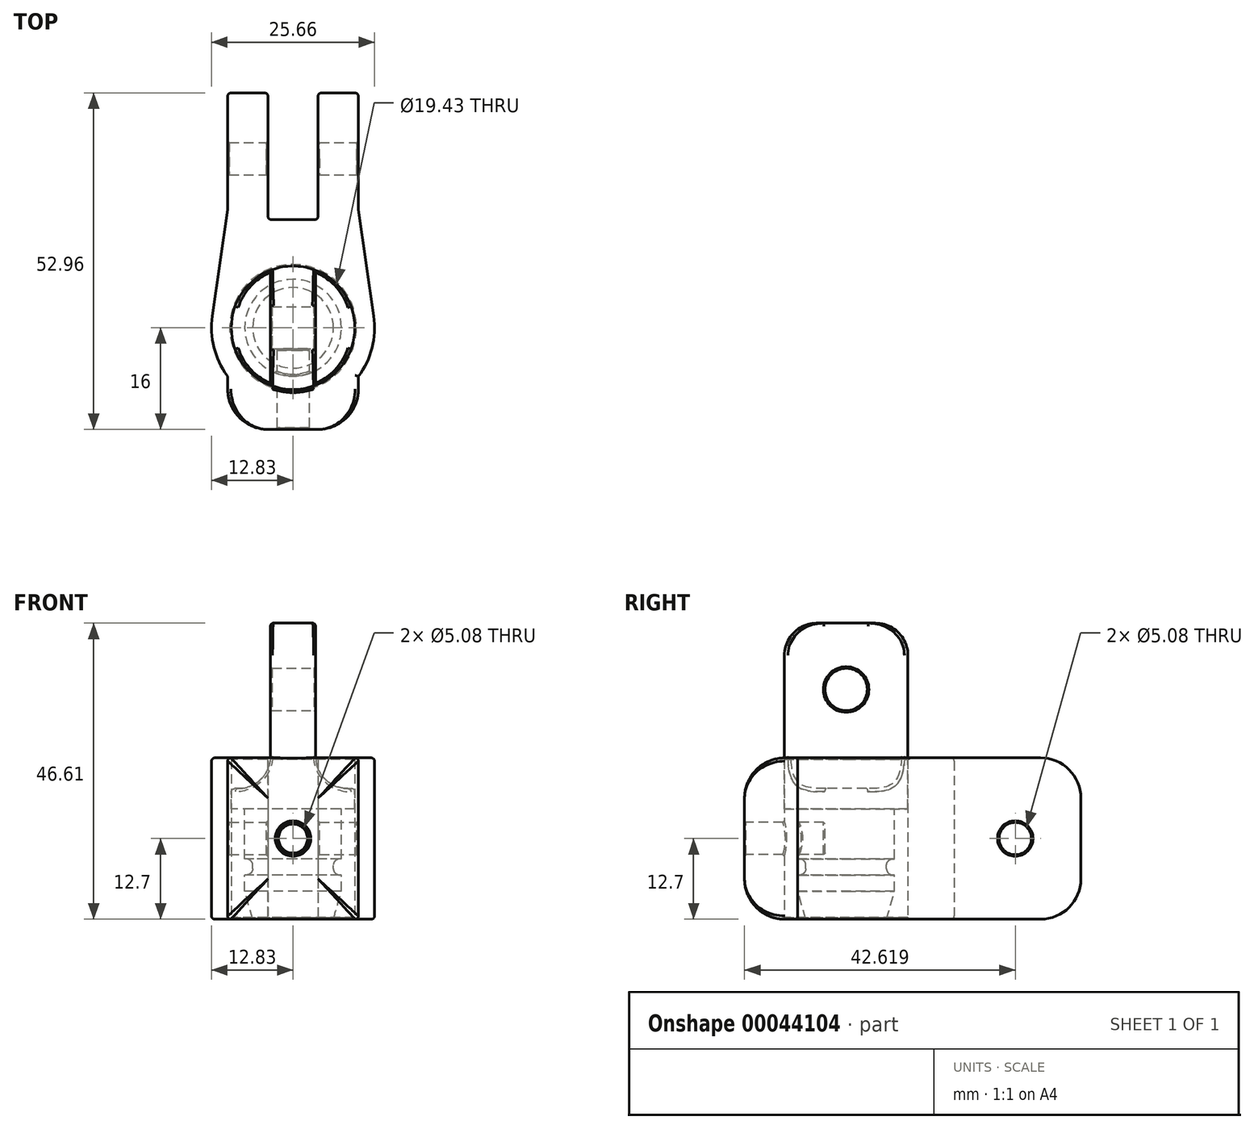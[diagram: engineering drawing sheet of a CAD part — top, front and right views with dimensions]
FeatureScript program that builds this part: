
annotation { "Feature Type Name" : "Feature", "Feature Type Description" : "" }
export const myFeature = defineFeature(function(context is Context, id is Id, definition is map)
    precondition{}
    {
        {
            var Q0;
            Q0=qCreatedBy(makeId("Front.planeOp"),FACE);
            var sketch = newSketch(context, id + "F0", { "sketchPlane" : qUnion([Q0])});
            skLineSegment(sketch, "E0", {"start": v(0, 0) * mm, "end": v(-6.35, 0) * mm});
            skLineSegment(sketch, "E1", {"start": v(-6.35, 0) * mm, "end": v(-7.62, 4.42) * mm});
            skLineSegment(sketch, "E2", {"start": v(-7.62, 4.42) * mm, "end": v(-7.62, 6.96) * mm});
            skLineSegment(sketch, "E3", {"start": v(-7.62, 6.96) * mm, "end": v(-7.37, 6.96) * mm});
            skLineSegment(sketch, "E4", {"start": v(-6.35, 7.98) * mm, "end": v(-6.35, 8.48) * mm});
            skLineSegment(sketch, "E5", {"start": v(-7.37, 9.5) * mm, "end": v(-7.62, 9.5) * mm});
            skLineSegment(sketch, "E6", {"start": v(-7.62, 9.5) * mm, "end": v(-7.62, 17.37) * mm});
            skLineSegment(sketch, "E7", {"start": v(0, 17.37) * mm, "end": v(-9.72, 17.37) * mm});
            skLineSegment(sketch, "E8", {"start": v(-9.72, 17.37) * mm, "end": v(-9.72, 37.08) * mm});
            skLineSegment(sketch, "E9", {"start": v(0, 46.6) * mm, "end": v(0, 46.6) * mm});
            skLineSegment(sketch, "E10", {"start": v(0, 46.6) * mm, "end": v(0, 0) * mm});
            skPoint(sketch, "E11.visualSharp", {"position": v(-9.72, 46.6) * mm});
            skPoint(sketch, "E12.visualSharp", {"position": v(-6.35, 9.5) * mm});
            skArc(sketch, "E12.filletArc", {"start": v(-6.35, 8.48) * mm, "mid": v(-6.65, 9.2) * mm, "end": v(-7.37, 9.5) * mm});
            skPoint(sketch, "E13.visualSharp", {"position": v(-6.35, 6.96) * mm});
            skArc(sketch, "E13.filletArc", {"start": v(-7.37, 6.96) * mm, "mid": v(-6.65, 7.26) * mm, "end": v(-6.35, 7.98) * mm});
            skLineSegment(sketch, "E14", {"start": v(0, 46.6) * mm, "end": v(-9.72, 46.6) * mm});
            skLineSegment(sketch, "E15", {"start": v(-9.72, 37.08) * mm, "end": v(-9.72, 46.6) * mm});
            skLineSegment(sketch, "E16", {"start": v(9.91, 20.55) * mm, "end": v(-9.72, 20.55) * mm, "construction": true});
            skSolve(sketch);
        }
        {
            var Q0;
            {var subQ4=sQuery(id+"F0.wireOp",EDGE,"E0");Q0=makeQuery(id+"F0.imprint","IMPRINT",FACE,{"disambiguationData":[TD([[makeQuery(id+"F0.imprint","IMPRINT",EDGE,{"derivedFrom":subQ4}),-1.0]])]});}
            var Q1;
            {var subQ0=sQuery(id+"F0.wireOp",EDGE,"E16");Q1=makeQuery(id+"F0.imprint","IMPRINT",FACE,{"disambiguationData":[TD([[makeQuery(id+"F0.imprint","IMPRINT",EDGE,{"derivedFrom":subQ0}),1.0]])]});}
            var Q2;
            {var subQ4=sQuery(id+"F0.wireOp",EDGE,"E14");Q2=makeQuery(id+"F0.imprint","IMPRINT",FACE,{"disambiguationData":[TD([[makeQuery(id+"F0.imprint","IMPRINT",EDGE,{"derivedFrom":subQ4}),1.0]])]});}
            var Q3;
            Q3=sQuery(id+"F0.wireOp",EDGE,"E10");
            revolve(context, id + "F1", {"entities" : qUnion([Q0, Q1, Q2]), "axis" : qUnion([Q3]), "revolveType" : RevolveType.FULL});
        }
        {
            var Q0;
            Q0=qCreatedBy(makeId("Front.planeOp"),FACE);
            var sketch = newSketch(context, id + "F2", { "sketchPlane" : qUnion([Q0])});
            skLineSegment(sketch, "E17.bottom", {"start": v(3.56, 48.33) * mm, "end": v(17.07, 48.33) * mm});
            skLineSegment(sketch, "E17.top", {"start": v(8.64, 20.57) * mm, "end": v(17.07, 20.57) * mm});
            skLineSegment(sketch, "E17.left", {"start": v(3.56, 48.33) * mm, "end": v(3.56, 25.65) * mm});
            skLineSegment(sketch, "E17.right", {"start": v(17.07, 48.33) * mm, "end": v(17.07, 20.57) * mm});
            skPoint(sketch, "E18.visualSharp", {"position": v(3.56, 20.57) * mm});
            skArc(sketch, "E18.filletArc", {"start": v(3.56, 25.65) * mm, "mid": v(5.04, 22.05) * mm, "end": v(8.64, 20.57) * mm});
            skLineSegment(sketch, "E19.MirrorCS", {"start": v(-3.56, 48.33) * mm, "end": v(-3.56, 25.65) * mm});
            skArc(sketch, "E20.MirrorCS", {"start": v(-3.56, 25.65) * mm, "mid": v(-5.04, 22.05) * mm, "end": v(-8.64, 20.57) * mm});
            skLineSegment(sketch, "E21.MirrorCS", {"start": v(-8.64, 20.57) * mm, "end": v(-17.07, 20.57) * mm});
            skLineSegment(sketch, "E22.MirrorCS", {"start": v(-17.07, 48.33) * mm, "end": v(-17.07, 20.57) * mm});
            skLineSegment(sketch, "E23.MirrorCS", {"start": v(-3.56, 48.33) * mm, "end": v(-17.07, 48.33) * mm});
            skSolve(sketch);
        }
        {
            var Q0;
            Q0 = qSketchRegion(id + "F2", true);
            extrude(context, id + "F3", {"entities" : qUnion([Q0]), "operationType" : NewBodyOperationType.REMOVE, "endBound" : BoundingType.SYMMETRIC, "oppositeDirection" : true, "depth" : 25.4 * mm});
        }
        {
            var Q0;
            Q0=makeQuery(id+"F3.boolean.opBoolean","SPLIT",EDGE,{"disambiguationData":[OD(1.0)],"derivedFrom":makeQuery(id+"F1.opRevolve","SWEPT_EDGE",EDGE,{"disambiguationData":[OSD([sQuery(id+"F0.wireOp",EDGE,"E14"),sQuery(id+"F0.wireOp",EDGE,"E15")])]})});
            var Q1;
            Q1=makeQuery(id+"F3.boolean.opBoolean","SPLIT",EDGE,{"disambiguationData":[OD(0.0)],"derivedFrom":makeQuery(id+"F1.opRevolve","SWEPT_EDGE",EDGE,{"disambiguationData":[OSD([sQuery(id+"F0.wireOp",EDGE,"E14"),sQuery(id+"F0.wireOp",EDGE,"E15")])]})});
            fillet(context, id + "F4", {"entities" : qUnion([Q0, Q1]), "radius" : 5.08 * mm, "tangentPropagation" : true, "allowEdgeOverflow" : false});
        }
        {
            var Q0;
            Q0=qCreatedBy(makeId("Right.planeOp"),FACE);
            var sketch = newSketch(context, id + "F5", { "sketchPlane" : qUnion([Q0])});
            skCircle(sketch, "E24", {"center": v(0, 36.17) * mm, "radius": 3.33 * mm});
            skSolve(sketch);
        }
        {
            var Q0;
            Q0 = qSketchRegion(id + "F5", true);
            extrude(context, id + "F6", {"entities" : qUnion([Q0]), "operationType" : NewBodyOperationType.REMOVE, "endBound" : BoundingType.SYMMETRIC, "oppositeDirection" : true, "depth" : 42.5 * mm});
        }
        {
            var Q0;
            Q0=makeQuery(id+"F6.boolean.opBoolean","COPY",FACE,{"derivedFrom":makeQuery(id+"F6.opExtrude","SWEPT_FACE",FACE,{"disambiguationData":[OSD([sQuery(id+"F5.wireOp",EDGE,"E24")])]})});
            chamfer(context, id + "F7", {"entities" : qUnion([Q0]), "width" : 0.25 * mm, "tangentPropagation" : true});
        }
        {
            var Q0;
            Q0=makeQuery(id+"F3.boolean.opBoolean","INTERSECT",EDGE,{"disambiguationData":[OD(1.0)],"derivedFrom":[makeQuery(id+"F1.opRevolve","SWEPT_FACE",FACE,{"disambiguationData":[OSD([sQuery(id+"F0.wireOp",EDGE,"E8"),sQuery(id+"F0.wireOp",EDGE,"E15")])]}),makeQuery(id+"F3.opExtrude","SWEPT_FACE",FACE,{"disambiguationData":[OSD([sQuery(id+"F2.wireOp",EDGE,"E18.filletArc")])]})]});
            var Q1;
            Q1=makeQuery(id+"F3.boolean.opBoolean","INTERSECT",EDGE,{"disambiguationData":[OD(1.0)],"derivedFrom":[makeQuery(id+"F1.opRevolve","SWEPT_FACE",FACE,{"disambiguationData":[OSD([sQuery(id+"F0.wireOp",EDGE,"E8"),sQuery(id+"F0.wireOp",EDGE,"E15")])]}),makeQuery(id+"F3.opExtrude","SWEPT_FACE",FACE,{"disambiguationData":[OSD([sQuery(id+"F2.wireOp",EDGE,"E17.left")])]})]});
            var Q2;
            Q2=makeQuery(id+"F4.opFillet","BLEND_EDGE",EDGE,{"blendedFrom":[makeQuery(id+"F3.boolean.opBoolean","SPLIT",EDGE,{"disambiguationData":[OD(1.0)],"derivedFrom":makeQuery(id+"F1.opRevolve","SWEPT_EDGE",EDGE,{"disambiguationData":[OSD([sQuery(id+"F0.wireOp",EDGE,"E14"),sQuery(id+"F0.wireOp",EDGE,"E15")])]})}),makeQuery(id+"F3.boolean.opBoolean","COPY",FACE,{"derivedFrom":makeQuery(id+"F3.opExtrude","SWEPT_FACE",FACE,{"disambiguationData":[OSD([sQuery(id+"F2.wireOp",EDGE,"E17.left")])]})})],"blendedInto":[makeQuery(id+"F3.boolean.opBoolean","COPY",FACE,{"derivedFrom":makeQuery(id+"F3.opExtrude","SWEPT_FACE",FACE,{"disambiguationData":[OSD([sQuery(id+"F2.wireOp",EDGE,"E17.left")])]})})]});
            var Q3;
            Q3=makeQuery(id+"F3.boolean.opBoolean","INTERSECT",EDGE,{"derivedFrom":[makeQuery(id+"F1.opRevolve","SWEPT_FACE",FACE,{"disambiguationData":[OSD([sQuery(id+"F0.wireOp",EDGE,"E14")])]}),makeQuery(id+"F3.opExtrude","SWEPT_FACE",FACE,{"disambiguationData":[OSD([sQuery(id+"F2.wireOp",EDGE,"E17.left")])]})]});
            var Q4;
            {var subQ0=sQuery(id+"F0.wireOp",EDGE,"E14");Q4=makeQuery(id+"F4.opFillet","BLEND_EDGE",EDGE,{"blendedFrom":[makeQuery(id+"F3.boolean.opBoolean","SPLIT",EDGE,{"disambiguationData":[OD(0.0)],"derivedFrom":makeQuery(id+"F1.opRevolve","SWEPT_EDGE",EDGE,{"disambiguationData":[OSD([subQ0,sQuery(id+"F0.wireOp",EDGE,"E15")])]})}),makeQuery(id+"F1.opRevolve","SWEPT_FACE",FACE,{"disambiguationData":[OSD([subQ0])]})],"blendedInto":[makeQuery(id+"F1.opRevolve","SWEPT_FACE",FACE,{"disambiguationData":[OSD([subQ0])]})]});}
            var Q5;
            Q5=makeQuery(id+"F4.opFillet","BLEND_EDGE",EDGE,{"blendedFrom":[makeQuery(id+"F3.boolean.opBoolean","SPLIT",EDGE,{"disambiguationData":[OD(0.0)],"derivedFrom":makeQuery(id+"F1.opRevolve","SWEPT_EDGE",EDGE,{"disambiguationData":[OSD([sQuery(id+"F0.wireOp",EDGE,"E14"),sQuery(id+"F0.wireOp",EDGE,"E15")])]})}),makeQuery(id+"F3.boolean.opBoolean","COPY",FACE,{"derivedFrom":makeQuery(id+"F3.opExtrude","SWEPT_FACE",FACE,{"disambiguationData":[OSD([sQuery(id+"F2.wireOp",EDGE,"E19.MirrorCS")])]})})],"blendedInto":[makeQuery(id+"F3.boolean.opBoolean","COPY",FACE,{"derivedFrom":makeQuery(id+"F3.opExtrude","SWEPT_FACE",FACE,{"disambiguationData":[OSD([sQuery(id+"F2.wireOp",EDGE,"E19.MirrorCS")])]})})]});
            var Q6;
            Q6=makeQuery(id+"F3.boolean.opBoolean","INTERSECT",EDGE,{"disambiguationData":[OD(0.0)],"derivedFrom":[makeQuery(id+"F1.opRevolve","SWEPT_FACE",FACE,{"disambiguationData":[OSD([sQuery(id+"F0.wireOp",EDGE,"E8"),sQuery(id+"F0.wireOp",EDGE,"E15")])]}),makeQuery(id+"F3.opExtrude","SWEPT_FACE",FACE,{"disambiguationData":[OSD([sQuery(id+"F2.wireOp",EDGE,"E19.MirrorCS")])]})]});
            var Q7;
            Q7=makeQuery(id+"F3.boolean.opBoolean","INTERSECT",EDGE,{"disambiguationData":[OD(0.0)],"derivedFrom":[makeQuery(id+"F1.opRevolve","SWEPT_FACE",FACE,{"disambiguationData":[OSD([sQuery(id+"F0.wireOp",EDGE,"E8"),sQuery(id+"F0.wireOp",EDGE,"E15")])]}),makeQuery(id+"F3.opExtrude","SWEPT_FACE",FACE,{"disambiguationData":[OSD([sQuery(id+"F2.wireOp",EDGE,"E20.MirrorCS")])]})]});
            var Q8;
            Q8=makeQuery(id+"F4.opFillet","BLEND_EDGE",EDGE,{"blendedFrom":[makeQuery(id+"F3.boolean.opBoolean","SPLIT",EDGE,{"disambiguationData":[OD(0.0)],"derivedFrom":makeQuery(id+"F1.opRevolve","SWEPT_EDGE",EDGE,{"disambiguationData":[OSD([sQuery(id+"F0.wireOp",EDGE,"E14"),sQuery(id+"F0.wireOp",EDGE,"E15")])]})}),makeQuery(id+"F3.boolean.opBoolean","COPY",FACE,{"derivedFrom":makeQuery(id+"F3.opExtrude","SWEPT_FACE",FACE,{"disambiguationData":[OSD([sQuery(id+"F2.wireOp",EDGE,"E17.left")])]})})],"blendedInto":[makeQuery(id+"F3.boolean.opBoolean","COPY",FACE,{"derivedFrom":makeQuery(id+"F3.opExtrude","SWEPT_FACE",FACE,{"disambiguationData":[OSD([sQuery(id+"F2.wireOp",EDGE,"E17.left")])]})})]});
            var Q9;
            Q9=makeQuery(id+"F3.boolean.opBoolean","INTERSECT",EDGE,{"disambiguationData":[OD(0.0)],"derivedFrom":[makeQuery(id+"F1.opRevolve","SWEPT_FACE",FACE,{"disambiguationData":[OSD([sQuery(id+"F0.wireOp",EDGE,"E8"),sQuery(id+"F0.wireOp",EDGE,"E15")])]}),makeQuery(id+"F3.opExtrude","SWEPT_FACE",FACE,{"disambiguationData":[OSD([sQuery(id+"F2.wireOp",EDGE,"E18.filletArc")])]})]});
            var Q10;
            Q10=makeQuery(id+"F3.boolean.opBoolean","INTERSECT",EDGE,{"disambiguationData":[OD(0.0)],"derivedFrom":[makeQuery(id+"F1.opRevolve","SWEPT_FACE",FACE,{"disambiguationData":[OSD([sQuery(id+"F0.wireOp",EDGE,"E8"),sQuery(id+"F0.wireOp",EDGE,"E15")])]}),makeQuery(id+"F3.opExtrude","SWEPT_FACE",FACE,{"disambiguationData":[OSD([sQuery(id+"F2.wireOp",EDGE,"E17.left")])]})]});
            var Q11;
            Q11=makeQuery(id+"F3.boolean.opBoolean","INTERSECT",EDGE,{"disambiguationData":[OD(1.0)],"derivedFrom":[makeQuery(id+"F1.opRevolve","SWEPT_FACE",FACE,{"disambiguationData":[OSD([sQuery(id+"F0.wireOp",EDGE,"E8"),sQuery(id+"F0.wireOp",EDGE,"E15")])]}),makeQuery(id+"F3.opExtrude","SWEPT_FACE",FACE,{"disambiguationData":[OSD([sQuery(id+"F2.wireOp",EDGE,"E20.MirrorCS")])]})]});
            var Q12;
            Q12=makeQuery(id+"F3.boolean.opBoolean","INTERSECT",EDGE,{"disambiguationData":[OD(1.0)],"derivedFrom":[makeQuery(id+"F1.opRevolve","SWEPT_FACE",FACE,{"disambiguationData":[OSD([sQuery(id+"F0.wireOp",EDGE,"E8"),sQuery(id+"F0.wireOp",EDGE,"E15")])]}),makeQuery(id+"F3.opExtrude","SWEPT_FACE",FACE,{"disambiguationData":[OSD([sQuery(id+"F2.wireOp",EDGE,"E19.MirrorCS")])]})]});
            var Q13;
            Q13=makeQuery(id+"F4.opFillet","BLEND_EDGE",EDGE,{"blendedFrom":[makeQuery(id+"F3.boolean.opBoolean","SPLIT",EDGE,{"disambiguationData":[OD(1.0)],"derivedFrom":makeQuery(id+"F1.opRevolve","SWEPT_EDGE",EDGE,{"disambiguationData":[OSD([sQuery(id+"F0.wireOp",EDGE,"E14"),sQuery(id+"F0.wireOp",EDGE,"E15")])]})}),makeQuery(id+"F3.boolean.opBoolean","COPY",FACE,{"derivedFrom":makeQuery(id+"F3.opExtrude","SWEPT_FACE",FACE,{"disambiguationData":[OSD([sQuery(id+"F2.wireOp",EDGE,"E19.MirrorCS")])]})})],"blendedInto":[makeQuery(id+"F3.boolean.opBoolean","COPY",FACE,{"derivedFrom":makeQuery(id+"F3.opExtrude","SWEPT_FACE",FACE,{"disambiguationData":[OSD([sQuery(id+"F2.wireOp",EDGE,"E19.MirrorCS")])]})})]});
            fillet(context, id + "F8", {"entities" : qUnion([Q0, Q1, Q2, Q3, Q4, Q5, Q6, Q7, Q8, Q9, Q10, Q11, Q12, Q13]), "radius" : 0.5 * mm, "tangentPropagation" : true, "allowEdgeOverflow" : false});
        }
        {
            var Q0;
            Q0=qCreatedBy(makeId("Top.planeOp"),FACE);
            var sketch = newSketch(context, id + "F9", { "sketchPlane" : qUnion([Q0])});
            skCircle(sketch, "E25", {"center": v(0, 0) * mm, "radius": 9.72 * mm});
            skCircle(sketch, "E26", {"center": v(0, 0) * mm, "radius": 12.83 * mm});
            skLineSegment(sketch, "E27", {"start": v(-10.29, 36.96) * mm, "end": v(-3.94, 36.96) * mm});
            skLineSegment(sketch, "E28", {"start": v(-3.94, 36.96) * mm, "end": v(-3.94, 17.02) * mm});
            skLineSegment(sketch, "E29", {"start": v(-3.94, 17.02) * mm, "end": v(3.94, 17.02) * mm});
            skLineSegment(sketch, "E30", {"start": v(3.94, 17.02) * mm, "end": v(3.94, 36.96) * mm});
            skLineSegment(sketch, "E31", {"start": v(3.94, 36.96) * mm, "end": v(10.29, 36.96) * mm});
            skLineSegment(sketch, "E32", {"start": v(10.29, 36.96) * mm, "end": v(10.29, 18.64) * mm});
            skLineSegment(sketch, "E33", {"start": v(10.29, 18.64) * mm, "end": v(12.7, 1.82) * mm});
            skLineSegment(sketch, "E34.MirrorCS", {"start": v(-10.29, 36.96) * mm, "end": v(-10.29, 18.64) * mm});
            skLineSegment(sketch, "E35.MirrorCS", {"start": v(-10.29, 18.64) * mm, "end": v(-12.7, 1.82) * mm});
            skLineSegment(sketch, "E36", {"start": v(-10.29, 26.57) * mm, "end": v(10.29, 26.57) * mm, "construction": true});
            skLineSegment(sketch, "E37", {"start": v(10.29, -16) * mm, "end": v(-10.29, -16) * mm});
            skLineSegment(sketch, "E38", {"start": v(-12.83, 0) * mm, "end": v(-12.83, 0) * mm});
            skLineSegment(sketch, "E39", {"start": v(12.83, 0) * mm, "end": v(12.83, 0) * mm});
            skLineSegment(sketch, "E40", {"start": v(-10.29, -7.66) * mm, "end": v(-10.29, -16) * mm});
            skLineSegment(sketch, "E41", {"start": v(10.29, -7.66) * mm, "end": v(10.29, -16) * mm});
            skSolve(sketch);
        }
        {
            var Q0;
            Q0=makeQuery(id+"F9.imprint","IMPRINT",FACE,{"disambiguationData":[TD([[makeQuery(id+"F9.imprint","IMPRINT",EDGE,{"derivedFrom":sQuery(id+"F9.wireOp",EDGE,"9beef8d4-fd38-4892-9b5a-89d50c57ea27.bottom")}),-1.0]])]});
            var Q1;
            {var subQ4=sQuery(id+"F9.wireOp",EDGE,"E27");Q1=makeQuery(id+"F9.imprint","IMPRINT",FACE,{"disambiguationData":[TD([[makeQuery(id+"F9.imprint","IMPRINT",EDGE,{"derivedFrom":subQ4}),-1.0]])]});}
            var Q2;
            Q2=makeQuery(id+"F9.imprint","IMPRINT",FACE,{"disambiguationData":[TD([[makeQuery(id+"F9.imprint","IMPRINT",EDGE,{"derivedFrom":sQuery(id+"F9.wireOp",EDGE,"E25")}),-1.0]])]});
            var Q3;
            Q3=makeQuery(id+"F9.imprint","IMPRINT",FACE,{"disambiguationData":[TD([[makeQuery(id+"F9.imprint","IMPRINT",EDGE,{"derivedFrom":sQuery(id+"F9.wireOp",EDGE,"E37")}),-1.0]])]});
            extrude(context, id + "F10", {"entities" : qUnion([Q0, Q1, Q2, Q3]), "depth" : 25.4 * mm});
        }
        {
            var Q0;
            Q0=makeQuery(id+"F10.opExtrude","SWEPT_FACE",FACE,{"disambiguationData":[OSD([sQuery(id+"F9.wireOp",EDGE,"E32")])]});
            var sketch = newSketch(context, id + "F11", { "sketchPlane" : qUnion([Q0])});
            skLineSegment(sketch, "E42", {"start": v(18.64, 12.7) * mm, "end": v(36.96, 12.7) * mm, "construction": true});
            skLineSegment(sketch, "E43", {"start": v(26.62, 25.4) * mm, "end": v(26.62, 0) * mm, "construction": true});
            skCircle(sketch, "E44", {"center": v(26.62, 12.7) * mm, "radius": 2.54 * mm});
            skSolve(sketch);
        }
        {
            var Q0;
            Q0=makeQuery(id+"F11.imprint","IMPRINT",FACE,{"disambiguationData":[TD([[makeQuery(id+"F11.imprint","IMPRINT",EDGE,{"derivedFrom":sQuery(id+"F11.wireOp",EDGE,"E44")}),1.0]])]});
            var Q1;
            Q1=sQuery(id+"F11.wireOp",EDGE,"E44");
            extrude(context, id + "F12", {"entities" : qUnion([Q0]), "operationType" : NewBodyOperationType.REMOVE, "surfaceEntities" : qUnion([Q1]), "oppositeDirection" : true, "depth" : 25.4 * mm});
        }
        {
            var Q0;
            Q0=makeQuery(id+"F10.opExtrude","SWEPT_FACE",FACE,{"disambiguationData":[OSD([sQuery(id+"F9.wireOp",EDGE,"E37")])]});
            var sketch = newSketch(context, id + "F13", { "sketchPlane" : qUnion([Q0])});
            skLineSegment(sketch, "E45", {"start": v(0, 0) * mm, "end": v(0, 25.4) * mm, "construction": true});
            skLineSegment(sketch, "E46", {"start": v(10.29, 12.7) * mm, "end": v(-10.29, 12.7) * mm, "construction": true});
            skCircle(sketch, "E47", {"center": v(0, 12.7) * mm, "radius": 2.54 * mm});
            skSolve(sketch);
        }
        {
            var Q0;
            Q0=makeQuery(id+"F13.imprint","IMPRINT",FACE,{"disambiguationData":[TD([[makeQuery(id+"F13.imprint","IMPRINT",EDGE,{"derivedFrom":sQuery(id+"F13.wireOp",EDGE,"E47")}),1.0]])]});
            extrude(context, id + "F14", {"entities" : qUnion([Q0]), "operationType" : NewBodyOperationType.REMOVE, "oppositeDirection" : true, "depth" : 12.7 * mm});
        }
        {
            var Q0;
            Q0=makeQuery(id+"F12.boolean.opBoolean","COPY",FACE,{"disambiguationData":[OD(0.0)],"derivedFrom":makeQuery(id+"F12.opExtrude","SWEPT_FACE",FACE,{"disambiguationData":[OSD([sQuery(id+"F11.wireOp",EDGE,"E44")])]})});
            var Q1;
            Q1=makeQuery(id+"F12.boolean.opBoolean","COPY",FACE,{"disambiguationData":[OD(1.0)],"derivedFrom":makeQuery(id+"F12.opExtrude","SWEPT_FACE",FACE,{"disambiguationData":[OSD([sQuery(id+"F11.wireOp",EDGE,"E44")])]})});
            var Q2;
            Q2=makeQuery(id+"F14.boolean.opBoolean","COPY",FACE,{"derivedFrom":makeQuery(id+"F14.opExtrude","SWEPT_FACE",FACE,{"disambiguationData":[OSD([sQuery(id+"F13.wireOp",EDGE,"E47")])]})});
            var Q3;
            Q3=makeQuery(id+"F10.opExtrude","SWEPT_FACE",FACE,{"disambiguationData":[OSD([sQuery(id+"F9.wireOp",EDGE,"E25")])]});
            chamfer(context, id + "F15", {"entities" : qUnion([Q0, Q1, Q2, Q3]), "width" : 0.25 * mm, "tangentPropagation" : true});
        }
        {
            var Q0;
            Q0=makeQuery(id+"F10.opExtrude","CAP_EDGE",EDGE,{"disambiguationData":[OSD([sQuery(id+"F9.wireOp",EDGE,"E27")])],"isStart":false});
            var Q1;
            Q1=makeQuery(id+"F10.opExtrude","CAP_EDGE",EDGE,{"disambiguationData":[OSD([sQuery(id+"F9.wireOp",EDGE,"E31")])],"isStart":false});
            var Q2;
            Q2=makeQuery(id+"F10.opExtrude","CAP_EDGE",EDGE,{"disambiguationData":[OSD([sQuery(id+"F9.wireOp",EDGE,"E31")])],"isStart":true});
            var Q3;
            Q3=makeQuery(id+"F10.opExtrude","CAP_EDGE",EDGE,{"disambiguationData":[OSD([sQuery(id+"F9.wireOp",EDGE,"E27")])],"isStart":true});
            var Q4;
            Q4=makeQuery(id+"F10.opExtrude","CAP_EDGE",EDGE,{"disambiguationData":[OSD([sQuery(id+"F9.wireOp",EDGE,"E37")])],"isStart":false});
            var Q5;
            Q5=makeQuery(id+"F10.opExtrude","SWEPT_EDGE",EDGE,{"disambiguationData":[OSD([sQuery(id+"F9.wireOp",EDGE,"E37"),sQuery(id+"F9.wireOp",EDGE,"E41")])]});
            var Q6;
            Q6=makeQuery(id+"F10.opExtrude","SWEPT_EDGE",EDGE,{"disambiguationData":[OSD([sQuery(id+"F9.wireOp",EDGE,"E37"),sQuery(id+"F9.wireOp",EDGE,"E40")])]});
            var Q7;
            Q7=makeQuery(id+"F10.opExtrude","CAP_EDGE",EDGE,{"disambiguationData":[OSD([sQuery(id+"F9.wireOp",EDGE,"E37")])],"isStart":true});
            fillet(context, id + "F16", {"entities" : qUnion([Q0, Q1, Q2, Q3, Q4, Q5, Q6, Q7]), "radius" : 6.35 * mm, "tangentPropagation" : true, "allowEdgeOverflow" : false});
        }
        {
            var Q0;
            Q0=makeQuery(id+"F10.opExtrude","SWEPT_FACE",FACE,{"disambiguationData":[OSD([sQuery(id+"F9.wireOp",EDGE,"E29")])]});
            var Q1;
            Q1=makeQuery(id+"F10.opExtrude","SWEPT_EDGE",EDGE,{"disambiguationData":[OSD([sQuery(id+"F9.wireOp",EDGE,"E30"),sQuery(id+"F9.wireOp",EDGE,"E31")])]});
            var Q2;
            Q2=makeQuery(id+"F10.opExtrude","SWEPT_EDGE",EDGE,{"disambiguationData":[OSD([sQuery(id+"F9.wireOp",EDGE,"E31"),sQuery(id+"F9.wireOp",EDGE,"E32")])]});
            var Q3;
            Q3=makeQuery(id+"F10.opExtrude","SWEPT_EDGE",EDGE,{"disambiguationData":[OSD([sQuery(id+"F9.wireOp",EDGE,"E27"),sQuery(id+"F9.wireOp",EDGE,"E28")])]});
            var Q4;
            Q4=makeQuery(id+"F10.opExtrude","SWEPT_EDGE",EDGE,{"disambiguationData":[OSD([sQuery(id+"F9.wireOp",EDGE,"E27"),sQuery(id+"F9.wireOp",EDGE,"E34.MirrorCS")])]});
            var Q5;
            Q5=makeQuery(id+"F10.opExtrude","SWEPT_FACE",FACE,{"disambiguationData":[OSD([sQuery(id+"F9.wireOp",EDGE,"E35.MirrorCS")])]});
            var Q6;
            {var subQ0=sQuery(id+"F9.wireOp",EDGE,"E26");Q6=makeQuery(id+"F10.opExtrude","SWEPT_FACE",FACE,{"disambiguationData":[OSD([subQ0]),TDD([makeQuery(id+"F9.imprint","IMPRINT",EDGE,{"disambiguationData":[TD([[makeQuery(id+"F9.imprint","INTERSECT",VERTEX,{"derivedFrom":[subQ0,sQuery(id+"F9.wireOp",EDGE,"E35.MirrorCS")]}),-1.0]])],"derivedFrom":subQ0})])]});}
            var Q7;
            Q7=makeQuery(id+"F10.opExtrude","SWEPT_FACE",FACE,{"disambiguationData":[OSD([sQuery(id+"F9.wireOp",EDGE,"E33")])]});
            var Q8;
            {var subQ0=sQuery(id+"F9.wireOp",EDGE,"E26");Q8=makeQuery(id+"F10.opExtrude","CAP_EDGE",EDGE,{"disambiguationData":[OSD([subQ0]),TDD([makeQuery(id+"F9.imprint","IMPRINT",EDGE,{"disambiguationData":[TD([[makeQuery(id+"F9.imprint","INTERSECT",VERTEX,{"derivedFrom":[subQ0,sQuery(id+"F9.wireOp",EDGE,"E33")]}),1.0]])],"derivedFrom":subQ0})])],"isStart":true});}
            var Q9;
            Q9=makeQuery(id+"F10.opExtrude","CAP_FACE",FACE,{"disambiguationData":[OSD([sQuery(id+"F9.wireOp",EDGE,"E25"),sQuery(id+"F9.wireOp",EDGE,"E26"),sQuery(id+"F9.wireOp",EDGE,"E27"),sQuery(id+"F9.wireOp",EDGE,"E28"),sQuery(id+"F9.wireOp",EDGE,"E29"),sQuery(id+"F9.wireOp",EDGE,"E30"),sQuery(id+"F9.wireOp",EDGE,"E31"),sQuery(id+"F9.wireOp",EDGE,"E32"),sQuery(id+"F9.wireOp",EDGE,"E33"),sQuery(id+"F9.wireOp",EDGE,"E34.MirrorCS"),sQuery(id+"F9.wireOp",EDGE,"E35.MirrorCS"),sQuery(id+"F9.wireOp",EDGE,"E37"),sQuery(id+"F9.wireOp",EDGE,"E40"),sQuery(id+"F9.wireOp",EDGE,"E41")])],"isStart":false});
            var Q10;
            Q10=makeQuery(id+"F10.opExtrude","CAP_EDGE",EDGE,{"disambiguationData":[OSD([sQuery(id+"F9.wireOp",EDGE,"E33")])],"isStart":true});
            var Q11;
            {var subQ0=sQuery(id+"F9.wireOp",EDGE,"E37");Q11=makeQuery(id+"F16.opFillet","BLEND_EDGE",EDGE,{"blendedFrom":[makeQuery(id+"F10.opExtrude","SWEPT_EDGE",EDGE,{"disambiguationData":[OSD([subQ0,sQuery(id+"F9.wireOp",EDGE,"E41")])]}),makeQuery(id+"F10.opExtrude","CAP_EDGE",EDGE,{"disambiguationData":[OSD([subQ0])],"isStart":true})],"blendedInto":[]});}
            var Q12;
            {var subQ0=sQuery(id+"F9.wireOp",EDGE,"E37");Q12=makeQuery(id+"F16.opFillet","BLEND_EDGE",EDGE,{"blendedFrom":[makeQuery(id+"F10.opExtrude","SWEPT_EDGE",EDGE,{"disambiguationData":[OSD([subQ0,sQuery(id+"F9.wireOp",EDGE,"E41")])]}),makeQuery(id+"F10.opExtrude","CAP_EDGE",EDGE,{"disambiguationData":[OSD([subQ0])],"isStart":false})],"blendedInto":[]});}
            var Q13;
            {var subQ0=sQuery(id+"F9.wireOp",EDGE,"E37");Q13=makeQuery(id+"F16.opFillet","BLEND_EDGE",EDGE,{"blendedFrom":[makeQuery(id+"F10.opExtrude","SWEPT_EDGE",EDGE,{"disambiguationData":[OSD([subQ0,sQuery(id+"F9.wireOp",EDGE,"E40")])]}),makeQuery(id+"F10.opExtrude","CAP_EDGE",EDGE,{"disambiguationData":[OSD([subQ0])],"isStart":false})],"blendedInto":[]});}
            var Q14;
            {var subQ0=sQuery(id+"F9.wireOp",EDGE,"E37");Q14=makeQuery(id+"F16.opFillet","BLEND_EDGE",EDGE,{"blendedFrom":[makeQuery(id+"F10.opExtrude","SWEPT_EDGE",EDGE,{"disambiguationData":[OSD([subQ0,sQuery(id+"F9.wireOp",EDGE,"E40")])]}),makeQuery(id+"F10.opExtrude","CAP_EDGE",EDGE,{"disambiguationData":[OSD([subQ0])],"isStart":true})],"blendedInto":[]});}
            fillet(context, id + "F17", {"entities" : qUnion([Q0, Q1, Q2, Q3, Q4, Q5, Q6, Q7, Q8, Q9, Q10, Q11, Q12, Q13, Q14]), "radius" : 0.5 * mm, "tangentPropagation" : true, "allowEdgeOverflow" : false});
        }
    });
